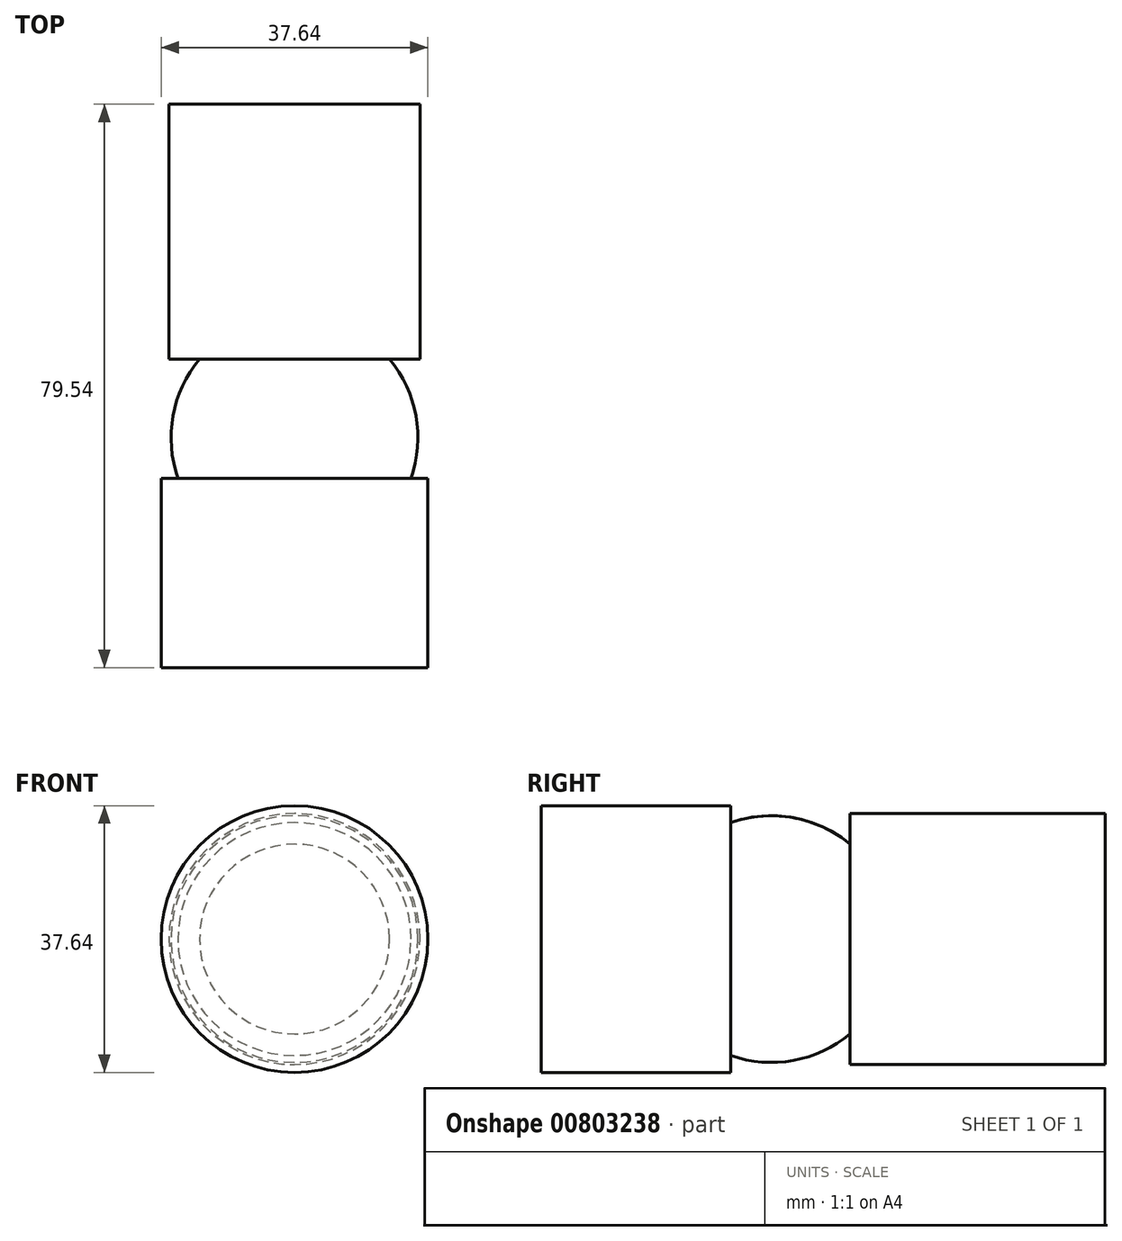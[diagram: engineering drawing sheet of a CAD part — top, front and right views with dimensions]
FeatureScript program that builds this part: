
annotation { "Feature Type Name" : "Feature", "Feature Type Description" : "" }
export const myFeature = defineFeature(function(context is Context, id is Id, definition is map)
    precondition{}
    {
        {
            var Q0;
            Q0=qCreatedBy(makeId("Top.planeOp"),FACE);
            var sketch = newSketch(context, id + "F0", { "sketchPlane" : qUnion([Q0])});
            skLineSegment(sketch, "E0", {"start": v(0, 71.57) * mm, "end": v(0, -55.81) * mm, "construction": true});
            skLineSegment(sketch, "E1.bottom", {"start": v(17.7, 15.4) * mm, "end": v(13.4, 15.4) * mm});
            skLineSegment(sketch, "E1.top", {"start": v(17.7, 51.36) * mm, "end": v(0, 51.36) * mm});
            skLineSegment(sketch, "E1.left", {"start": v(17.7, 15.4) * mm, "end": v(17.7, 51.36) * mm});
            skPoint(sketch, "E1.middle", {"position": v(0, 33.38) * mm});
            skArc(sketch, "E2", {"start": v(16.44, -1.48) * mm, "mid": v(17.14, 7.35) * mm, "end": v(13.4, 15.4) * mm});
            skLineSegment(sketch, "E3.bottom", {"start": v(0, -28.18) * mm, "end": v(18.82, -28.18) * mm});
            skLineSegment(sketch, "E3.top", {"start": v(16.44, -1.48) * mm, "end": v(18.82, -1.48) * mm});
            skLineSegment(sketch, "E3.left", {"start": v(0, -28.18) * mm, "end": v(0, -1.48) * mm});
            skLineSegment(sketch, "E3.right", {"start": v(18.82, -28.18) * mm, "end": v(18.82, -1.48) * mm});
            skPoint(sketch, "E1.right.end.orphan", {"position": v(-17.7, 51.36) * mm});
            skPoint(sketch, "E4.trimOffspring.end.orphan", {"position": v(-17.7, 15.4) * mm});
            skLineSegment(sketch, "E5", {"start": v(0, 51.36) * mm, "end": v(0, -28.18) * mm});
            skSolve(sketch);
        }
        {
            var Q0;
            Q0=makeQuery(id+"F0.imprint","IMPRINT",FACE,{"disambiguationData":[TD([[makeQuery(id+"F0.imprint","IMPRINT",EDGE,{"derivedFrom":sQuery(id+"F0.wireOp",EDGE,"E1.bottom")}),-1.0]])]});
            var Q1;
            Q1=sQuery(id+"F0.wireOp",EDGE,"E0");
            revolve(context, id + "F1", {"surfaceOperationType" : NewSurfaceOperationType.NEW, "entities" : qUnion([Q0]), "axis" : qUnion([Q1]), "revolveType" : RevolveType.FULL});
        }
    });
